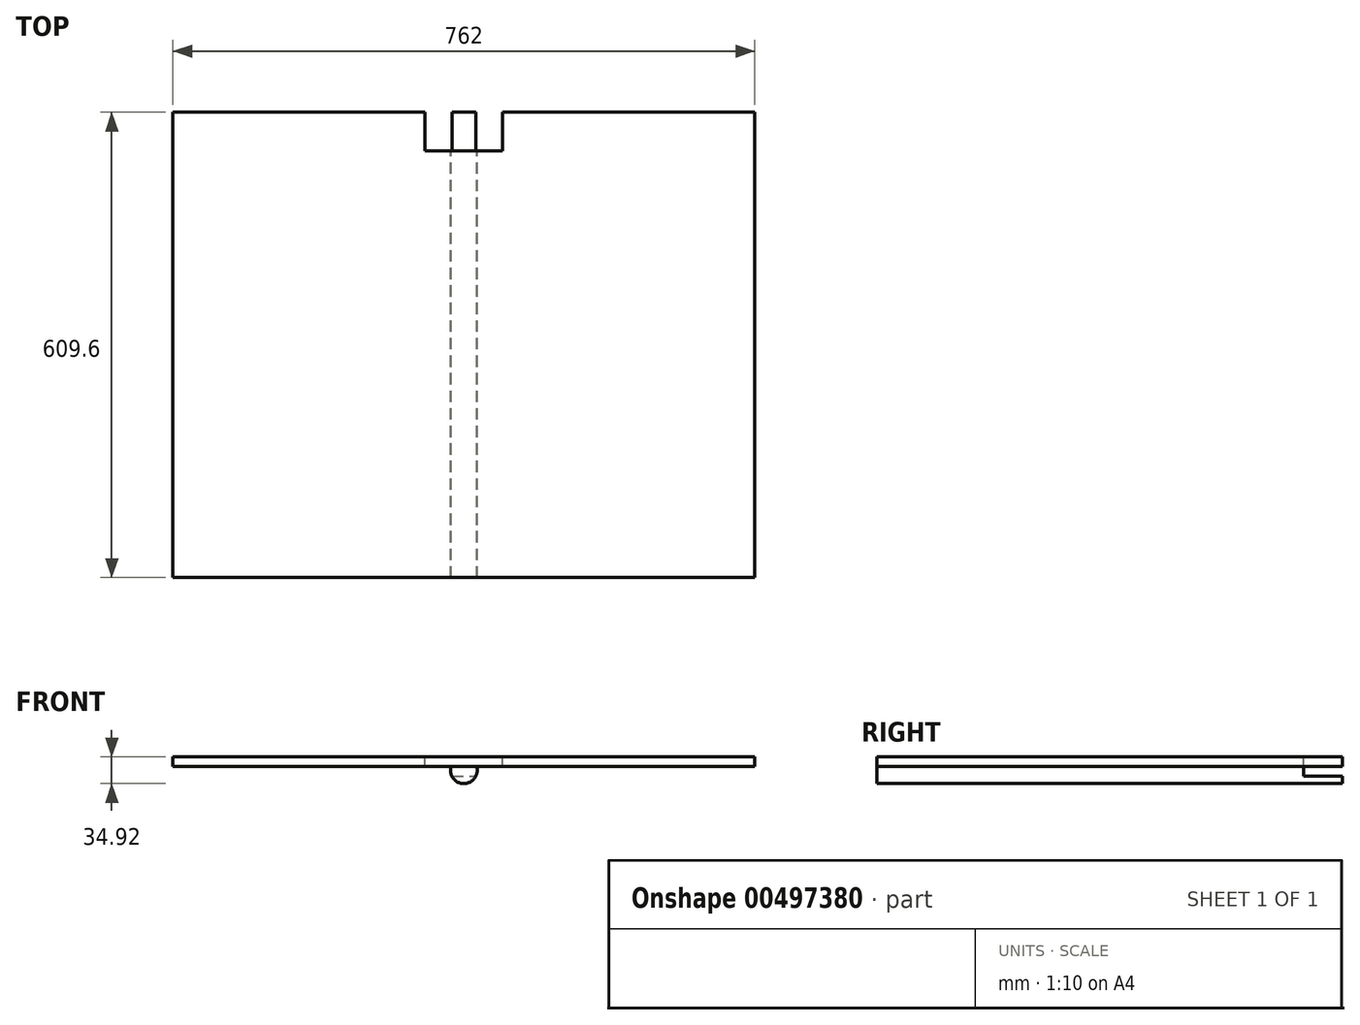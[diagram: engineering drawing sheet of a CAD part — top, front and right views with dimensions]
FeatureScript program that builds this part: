
annotation { "Feature Type Name" : "Feature", "Feature Type Description" : "" }
export const myFeature = defineFeature(function(context is Context, id is Id, definition is map)
    precondition{}
    {
        {
            var Q0;
            Q0=qCreatedBy(makeId("Front.planeOp"),FACE);
            var sketch = newSketch(context, id + "F0", { "sketchPlane" : qUnion([Q0])});
            skCircle(sketch, "E0", {"center": v(0, 0) * mm, "radius": 17.46 * mm});
            skSolve(sketch);
        }
        {
            var Q0;
            Q0 = qSketchRegion(id + "F0", true);
            extrude(context, id + "F1", {"entities" : qUnion([Q0]), "depth" : 50.8 * mm});
        }
        {
            var Q0;
            Q0=makeQuery(id+"F1.opExtrude","CAP_FACE",FACE,{"disambiguationData":[OSD([sQuery(id+"F0.wireOp",EDGE,"E0")])],"isStart":false});
            var sketch = newSketch(context, id + "F2", { "sketchPlane" : qUnion([Q0])});
            skLineSegment(sketch, "E1", {"start": v(-16.8, 4.76) * mm, "end": v(16.8, 4.76) * mm});
            skArc(sketch, "E2", {"start": v(-16.8, 4.76) * mm, "mid": v(0, -17.46) * mm, "end": v(16.8, 4.76) * mm});
            skSolve(sketch);
        }
        {
            var Q0;
            Q0 = qSketchRegion(id + "F2", true);
            extrude(context, id + "F3", {"entities" : qUnion([Q0]), "operationType" : NewBodyOperationType.ADD, "depth" : 558.8 * mm});
        }
        {
            var Q0;
            Q0=qCreatedBy(makeId("Front.planeOp"),FACE);
            var sketch = newSketch(context, id + "F4", { "sketchPlane" : qUnion([Q0])});
            skLineSegment(sketch, "E3.bottom", {"start": v(-381, 17.46) * mm, "end": v(381, 17.46) * mm});
            skLineSegment(sketch, "E3.top", {"start": v(-381, 4.76) * mm, "end": v(381, 4.76) * mm});
            skLineSegment(sketch, "E3.left", {"start": v(-381, 17.46) * mm, "end": v(-381, 4.76) * mm});
            skLineSegment(sketch, "E3.right", {"start": v(381, 17.46) * mm, "end": v(381, 4.76) * mm});
            skSolve(sketch);
        }
        {
            var Q0;
            Q0 = qSketchRegion(id + "F4", true);
            extrude(context, id + "F5", {"entities" : qUnion([Q0]), "depth" : 609.6 * mm});
        }
        {
            var Q0;
            Q0=makeQuery(id+"F5.opExtrude","SWEPT_FACE",FACE,{"disambiguationData":[OSD([sQuery(id+"F4.wireOp",EDGE,"E3.bottom")])]});
            var sketch = newSketch(context, id + "F6", { "sketchPlane" : qUnion([Q0])});
            skLineSegment(sketch, "E4.bottom", {"start": v(-50.8, 0) * mm, "end": v(50.8, 0) * mm});
            skLineSegment(sketch, "E4.top", {"start": v(-50.8, -50.8) * mm, "end": v(50.8, -50.8) * mm});
            skLineSegment(sketch, "E4.left", {"start": v(-50.8, 0) * mm, "end": v(-50.8, -50.8) * mm});
            skLineSegment(sketch, "E4.right", {"start": v(50.8, 0) * mm, "end": v(50.8, -50.8) * mm});
            skSolve(sketch);
        }
        {
            var Q0;
            Q0 = qSketchRegion(id + "F6", true);
            var Q1;
            Q1=makeQuery(id+"F3.boolean.opBoolean","MERGE",FACE,{"derivedFrom":[makeQuery(id+"F1.opExtrude","SWEPT_FACE",FACE,{"disambiguationData":[OSD([sQuery(id+"F0.wireOp",EDGE,"E0")])]}),makeQuery(id+"F3.opExtrude","SWEPT_FACE",FACE,{"disambiguationData":[OSD([sQuery(id+"F2.wireOp",EDGE,"E2")])]})]});
            extrude(context, id + "F7", {"entities" : qUnion([Q0]), "operationType" : NewBodyOperationType.REMOVE, "oppositeDirection" : true, "endBoundEntityFace" : qUnion([Q1]), "depth" : 25.4 * mm});
        }
    });
